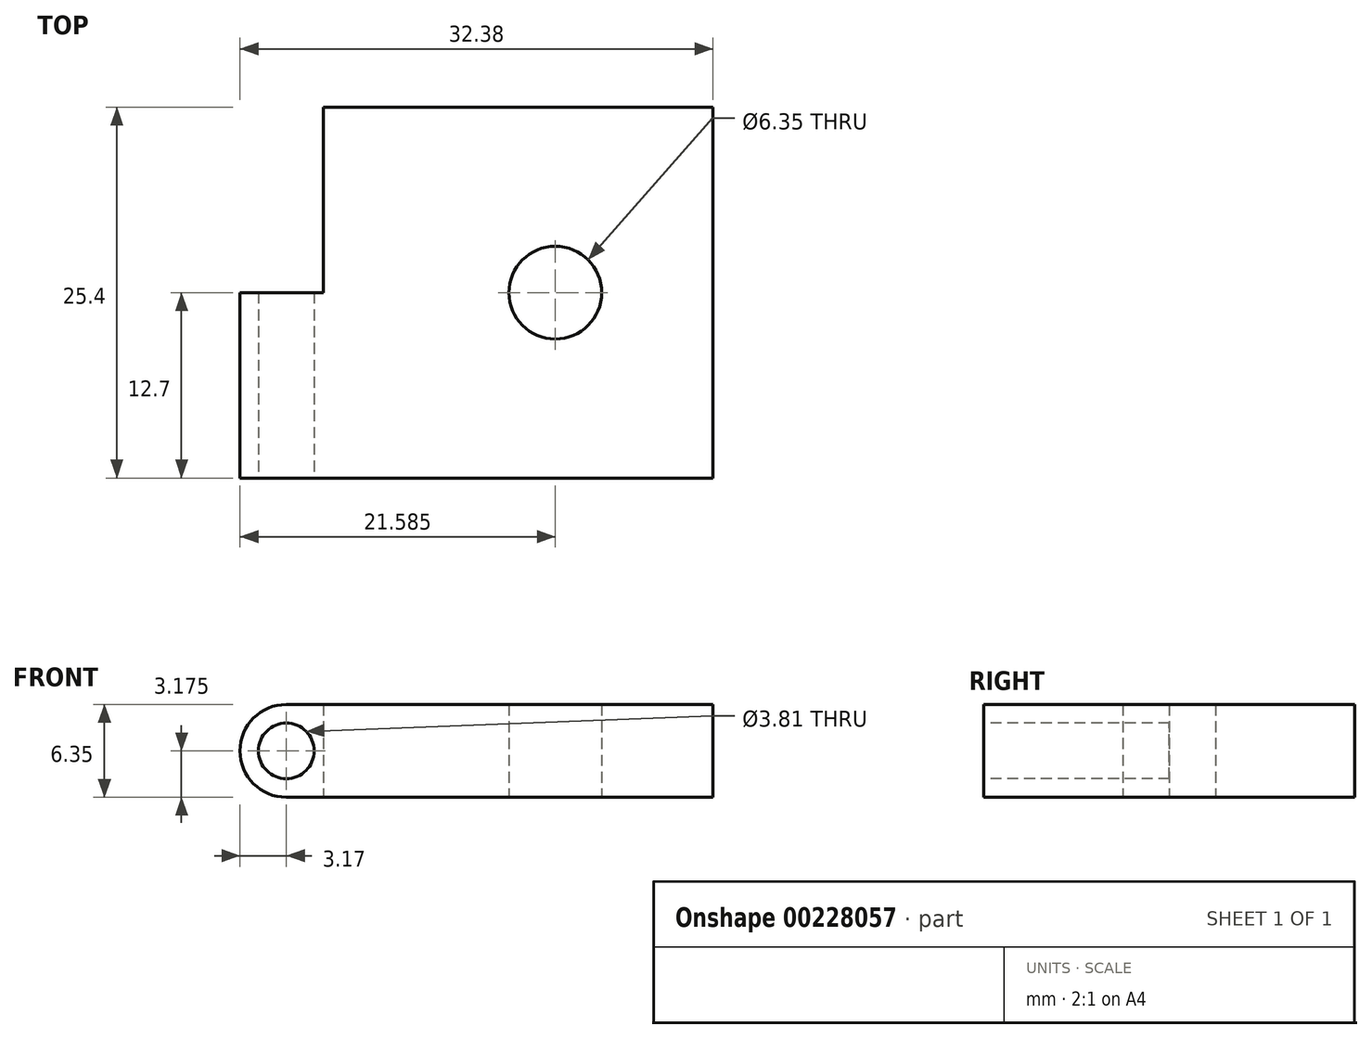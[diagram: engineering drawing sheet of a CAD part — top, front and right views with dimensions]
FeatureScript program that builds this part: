
annotation { "Feature Type Name" : "Feature", "Feature Type Description" : "" }
export const myFeature = defineFeature(function(context is Context, id is Id, definition is map)
    precondition{}
    {
        {
            var Q0;
            Q0=qCreatedBy(makeId("Top.planeOp"),FACE);
            var sketch = newSketch(context, id + "F0", { "sketchPlane" : qUnion([Q0])});
            skLineSegment(sketch, "E0.bottom", {"start": v(0, 0) * mm, "end": v(26.67, 0) * mm});
            skLineSegment(sketch, "E0.top", {"start": v(0, 25.4) * mm, "end": v(26.67, 25.4) * mm});
            skLineSegment(sketch, "E0.left", {"start": v(0, 0) * mm, "end": v(0, 25.4) * mm});
            skLineSegment(sketch, "E0.right", {"start": v(26.67, 0) * mm, "end": v(26.67, 25.4) * mm});
            skCircle(sketch, "E1", {"center": v(15.87, 12.7) * mm, "radius": 3.18 * mm});
            skLineSegment(sketch, "E2", {"start": v(15.87, 25.4) * mm, "end": v(15.87, 0) * mm, "construction": true});
            skSolve(sketch);
        }
        {
            var Q0;
            Q0 = qSketchRegion(id + "F0", true);
            extrude(context, id + "F1", {"entities" : qUnion([Q0]), "depth" : 6.35 * mm, "offsetDistance" : 25.4 * mm});
        }
        {
            var Q0;
            Q0=makeQuery(id+"F1.opExtrude","SWEPT_FACE",FACE,{"disambiguationData":[OSD([sQuery(id+"F0.wireOp",EDGE,"E0.bottom")])]});
            var sketch = newSketch(context, id + "F2", { "sketchPlane" : qUnion([Q0])});
            skLineSegment(sketch, "E3", {"start": v(0, 6.35) * mm, "end": v(0, 0) * mm});
            skLineSegment(sketch, "E4", {"start": v(0, 0) * mm, "end": v(-2.54, 0) * mm});
            skArc(sketch, "E5", {"start": v(-2.54, 6.35) * mm, "mid": v(-5.71, 3.17) * mm, "end": v(-2.54, 0) * mm});
            skLineSegment(sketch, "E6", {"start": v(0, 6.35) * mm, "end": v(-2.54, 6.35) * mm});
            skCircle(sketch, "E7", {"center": v(-2.54, 3.17) * mm, "radius": 1.9 * mm});
            skSolve(sketch);
        }
        {
            var Q0;
            Q0 = qSketchRegion(id + "F2", true);
            extrude(context, id + "F3", {"entities" : qUnion([Q0]), "operationType" : NewBodyOperationType.ADD, "oppositeDirection" : true, "depth" : 12.7 * mm, "offsetDistance" : 25.4 * mm});
        }
    });
